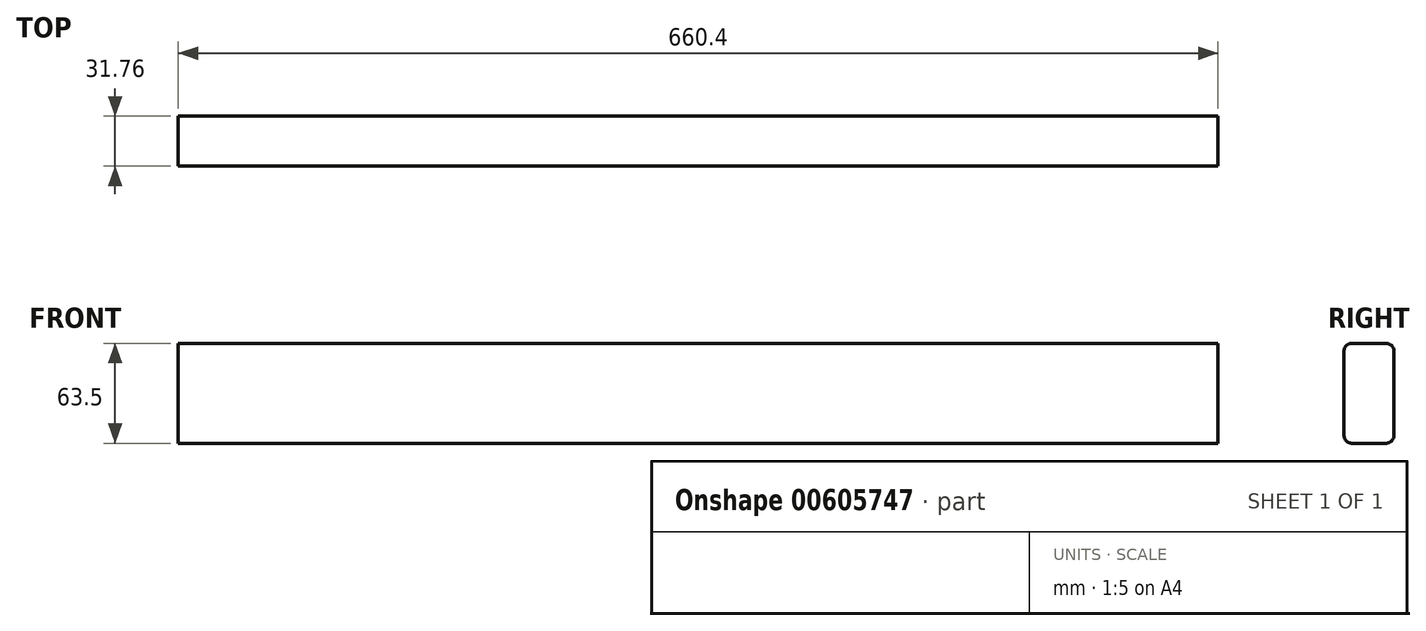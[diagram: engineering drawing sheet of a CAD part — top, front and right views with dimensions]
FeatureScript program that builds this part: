
annotation { "Feature Type Name" : "Feature", "Feature Type Description" : "" }
export const myFeature = defineFeature(function(context is Context, id is Id, definition is map)
    precondition{}
    {
        {
            var Q0;
            Q0=qCreatedBy(makeId("Right.planeOp"),FACE);
            var sketch = newSketch(context, id + "F0", { "sketchPlane" : qUnion([Q0])});
            skLineSegment(sketch, "E0.bottom", {"start": v(-15.87, 63.5) * mm, "end": v(15.88, 63.5) * mm});
            skLineSegment(sketch, "E0.top", {"start": v(-15.88, 127) * mm, "end": v(15.88, 127) * mm});
            skLineSegment(sketch, "E0.left", {"start": v(-15.87, 63.5) * mm, "end": v(-15.88, 127) * mm});
            skLineSegment(sketch, "E0.right", {"start": v(15.88, 63.5) * mm, "end": v(15.88, 127) * mm});
            skPoint(sketch, "E0.middle", {"position": v(0, 95.25) * mm});
            skSolve(sketch);
        }
        {
            var Q0;
            Q0 = qSketchRegion(id + "F0", true);
            extrude(context, id + "F1", {"entities" : qUnion([Q0]), "depth" : 660.4 * mm, "offsetDistance" : 25.4 * mm});
        }
        {
            var Q0;
            Q0=makeQuery(id+"F1.opExtrude","SWEPT_EDGE",EDGE,{"disambiguationData":[OSD([sQuery(id+"F0.wireOp",EDGE,"E0.top"),sQuery(id+"F0.wireOp",EDGE,"E0.right")])]});
            var Q1;
            Q1=makeQuery(id+"F1.opExtrude","SWEPT_EDGE",EDGE,{"disambiguationData":[OSD([sQuery(id+"F0.wireOp",EDGE,"E0.top"),sQuery(id+"F0.wireOp",EDGE,"E0.left")])]});
            var Q2;
            Q2=makeQuery(id+"F1.opExtrude","SWEPT_EDGE",EDGE,{"disambiguationData":[OSD([sQuery(id+"F0.wireOp",EDGE,"E0.bottom"),sQuery(id+"F0.wireOp",EDGE,"E0.left")])]});
            var Q3;
            Q3=makeQuery(id+"F1.opExtrude","SWEPT_EDGE",EDGE,{"disambiguationData":[OSD([sQuery(id+"F0.wireOp",EDGE,"E0.bottom"),sQuery(id+"F0.wireOp",EDGE,"E0.right")])]});
            fillet(context, id + "F2", {"entities" : qUnion([Q0, Q1, Q2, Q3]), "radius" : 5.08 * mm, "tangentPropagation" : true, "allowEdgeOverflow" : false});
        }
    });
